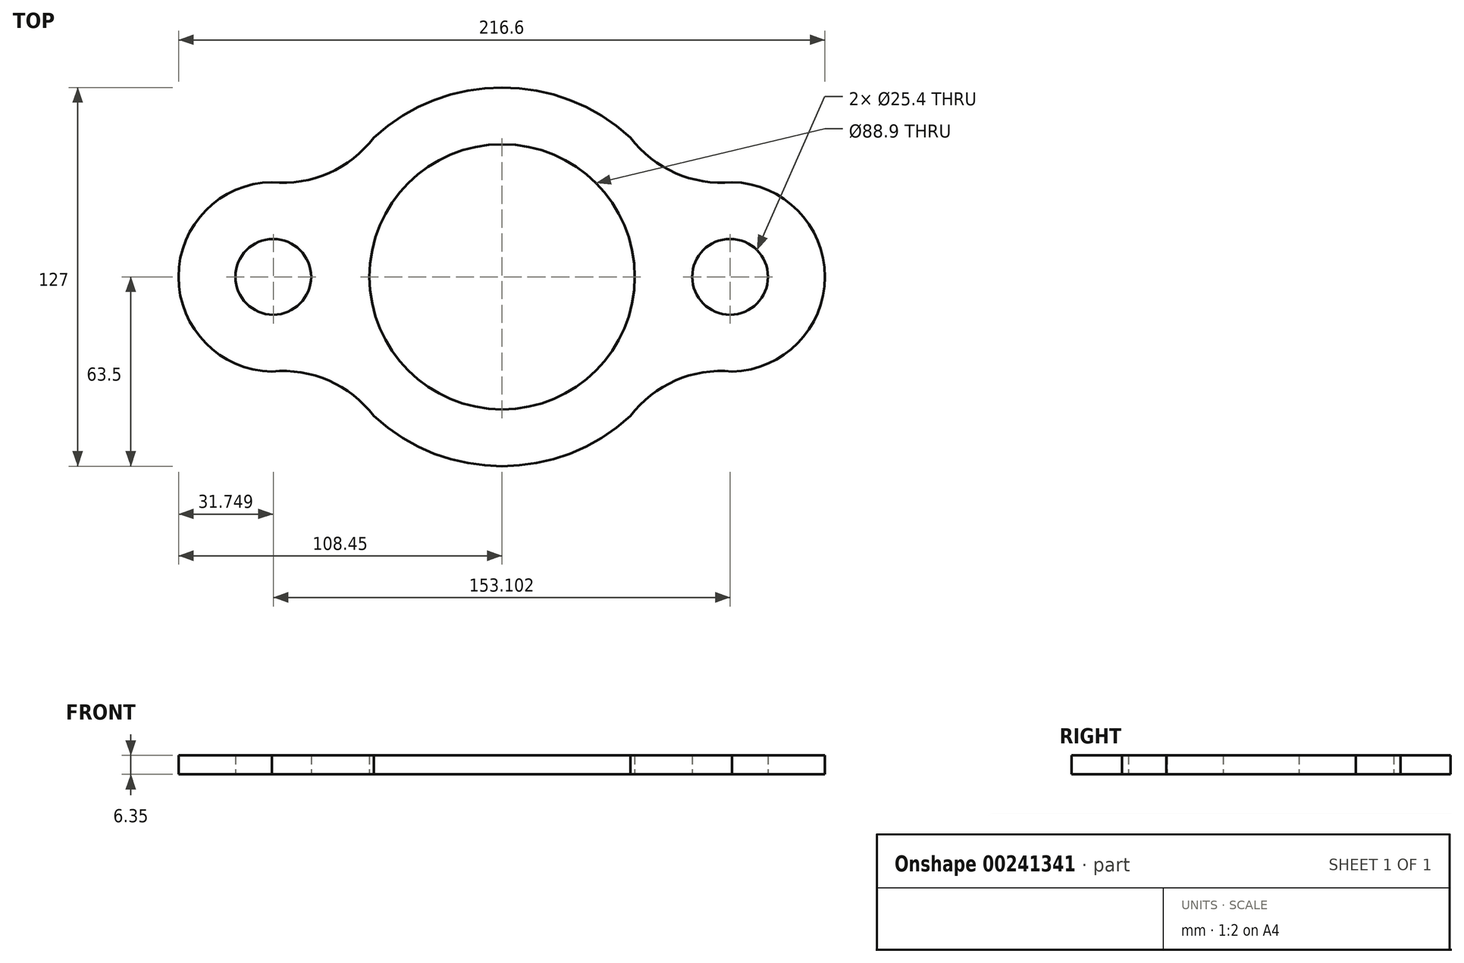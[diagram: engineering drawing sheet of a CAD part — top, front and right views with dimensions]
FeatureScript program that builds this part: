
annotation { "Feature Type Name" : "Feature", "Feature Type Description" : "" }
export const myFeature = defineFeature(function(context is Context, id is Id, definition is map)
    precondition{}
    {
        {
            var Q0;
            Q0=qCreatedBy(makeId("Top.planeOp"),FACE);
            var sketch = newSketch(context, id + "F0", { "sketchPlane" : qUnion([Q0])});
            skCircle(sketch, "E0", {"center": v(0, 0) * mm, "radius": 44.45 * mm});
            skCircle(sketch, "E1", {"center": v(-76.7, 0) * mm, "radius": 12.7 * mm});
            skCircle(sketch, "E2", {"center": v(76.4, 0) * mm, "radius": 12.7 * mm});
            skArc(sketch, "E3", {"start": v(-48.9, -40.5) * mm, "mid": v(0, -63.5) * mm, "end": v(48.9, -40.5) * mm});
            skArc(sketch, "E4", {"start": v(77.07, -31.74) * mm, "mid": v(108.09, 2.03) * mm, "end": v(73.02, 31.57) * mm});
            skArc(sketch, "E5", {"start": v(-73.3, 31.57) * mm, "mid": v(-108.45, 0) * mm, "end": v(-73.3, -31.57) * mm});
            skArc(sketch, "E6", {"start": v(-77.12, 31.75) * mm, "mid": v(-58.11, 34.78) * mm, "end": v(-43.01, 46.72) * mm});
            skArc(sketch, "E7.MirrorC", {"start": v(77.07, 31.74) * mm, "mid": v(58.09, 34.79) * mm, "end": v(43.01, 46.72) * mm});
            skArc(sketch, "E8.MirrorC", {"start": v(-77.12, -31.75) * mm, "mid": v(-58.11, -34.78) * mm, "end": v(-43.01, -46.72) * mm});
            skArc(sketch, "E9.MirrorC", {"start": v(77.07, -31.74) * mm, "mid": v(58.09, -34.79) * mm, "end": v(43.01, -46.72) * mm});
            skArc(sketch, "E10.trimOffspring", {"start": v(48.9, 40.5) * mm, "mid": v(0, 63.5) * mm, "end": v(-48.9, 40.5) * mm});
            skLineSegment(sketch, "E11", {"start": v(-76.7, 0) * mm, "end": v(0, 0) * mm});
            skLineSegment(sketch, "E12", {"start": v(-76.2, -66.3) * mm, "end": v(0, -66.3) * mm});
            skSolve(sketch);
        }
        {
            var Q0;
            Q0=makeQuery(id+"F0.imprint","IMPRINT",FACE,{"disambiguationData":[TD([[makeQuery(id+"F0.imprint","IMPRINT",EDGE,{"derivedFrom":sQuery(id+"F0.wireOp",EDGE,"E0")}),-1.0]])]});
            extrude(context, id + "F1", {"entities" : qUnion([Q0]), "depth" : 6.35 * mm});
        }
    });
